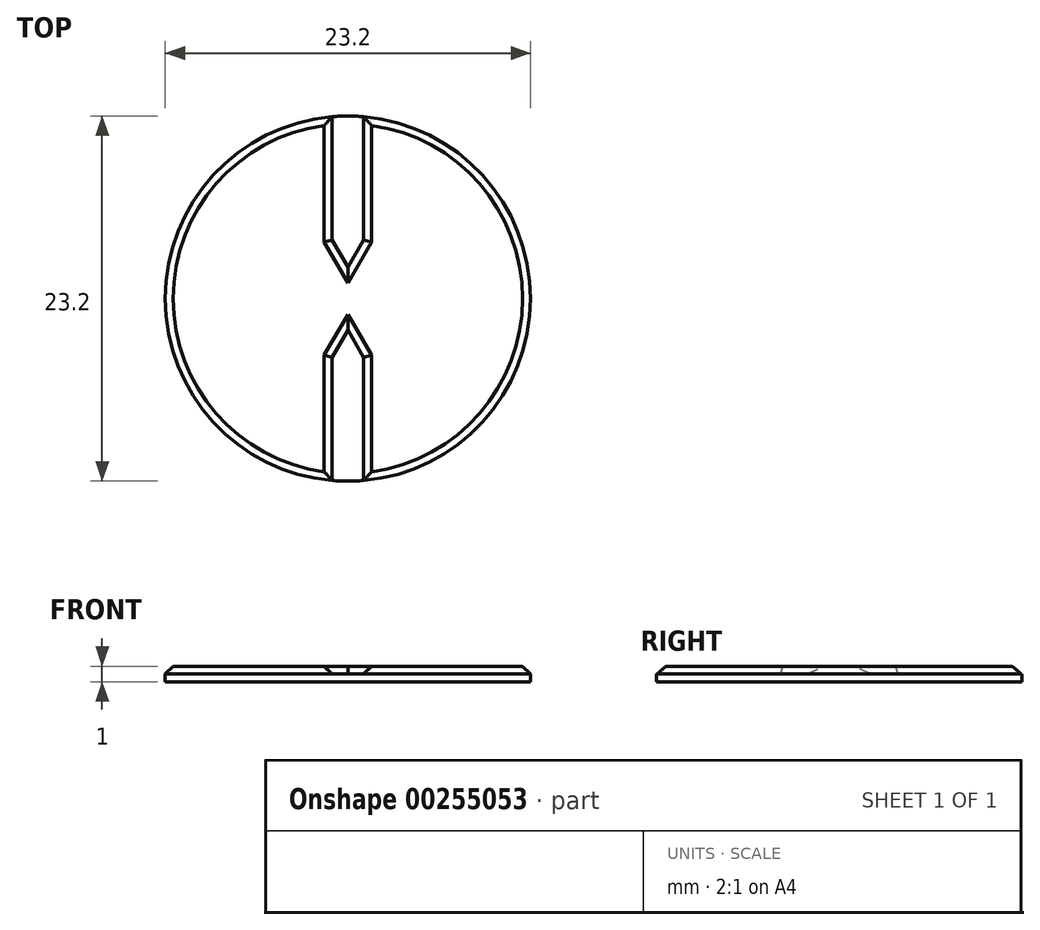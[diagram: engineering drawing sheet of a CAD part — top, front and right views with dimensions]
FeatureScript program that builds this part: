
annotation { "Feature Type Name" : "Feature", "Feature Type Description" : "" }
export const myFeature = defineFeature(function(context is Context, id is Id, definition is map)
    precondition{}
    {
        {
            var Q0;
            Q0=qCreatedBy(makeId("Top.planeOp"),FACE);
            var sketch = newSketch(context, id + "F0", { "sketchPlane" : qUnion([Q0])});
            skCircle(sketch, "E0", {"center": v(0, 0) * mm, "radius": 11.6 * mm});
            skSolve(sketch);
        }
        {
            var Q0;
            Q0 = qSketchRegion(id + "F0", true);
            extrude(context, id + "F1", {"entities" : qUnion([Q0]), "depth" : 1 * mm});
        }
        {
            var Q0;
            Q0=makeQuery(id+"F1.opExtrude","CAP_FACE",FACE,{"disambiguationData":[OSD([sQuery(id+"F0.wireOp",EDGE,"E0")])],"isStart":false});
            var sketch = newSketch(context, id + "F2", { "sketchPlane" : qUnion([Q0])});
            skLineSegment(sketch, "E1.bottom", {"start": v(1, -11.56) * mm, "end": v(-1, -11.56) * mm});
            skLineSegment(sketch, "E1.top", {"start": v(1, 11.56) * mm, "end": v(-1, 11.56) * mm});
            skLineSegment(sketch, "E1.left", {"start": v(1, -11.56) * mm, "end": v(1, 11.56) * mm});
            skLineSegment(sketch, "E1.right", {"start": v(-1, -11.56) * mm, "end": v(-1, 11.56) * mm});
            skPoint(sketch, "E1.middle", {"position": v(0, 0) * mm});
            skCircle(sketch, "E2.0.0", {"center": v(0, 0) * mm, "radius": 11.6 * mm});
            skLineSegment(sketch, "E3.1.0", {"start": v(4.91, -10.5) * mm, "end": v(-6.64, 9.5) * mm});
            skLineSegment(sketch, "E3.1.1", {"start": v(6.64, -9.5) * mm, "end": v(-4.91, 10.5) * mm});
            skLineSegment(sketch, "E3.2.0", {"start": v(9.5, -6.64) * mm, "end": v(-10.5, 4.91) * mm});
            skLineSegment(sketch, "E3.2.1", {"start": v(10.5, -4.91) * mm, "end": v(-9.5, 6.64) * mm});
            skLineSegment(sketch, "E3.3.0", {"start": v(11.56, -1) * mm, "end": v(-11.56, -1) * mm});
            skLineSegment(sketch, "E3.3.1", {"start": v(11.56, 1) * mm, "end": v(-11.56, 1) * mm});
            skLineSegment(sketch, "E3.4.0", {"start": v(10.5, 4.91) * mm, "end": v(-9.5, -6.64) * mm});
            skLineSegment(sketch, "E3.4.1", {"start": v(9.5, 6.64) * mm, "end": v(-10.5, -4.91) * mm});
            skLineSegment(sketch, "E3.5.0", {"start": v(6.64, 9.5) * mm, "end": v(-4.91, -10.5) * mm});
            skLineSegment(sketch, "E3.5.1", {"start": v(4.91, 10.5) * mm, "end": v(-6.64, -9.5) * mm});
            skLineSegment(sketch, "E3.6.0", {"start": v(1, 11.56) * mm, "end": v(1, -11.56) * mm});
            skLineSegment(sketch, "E3.6.1", {"start": v(-1, 11.56) * mm, "end": v(-1, -11.56) * mm});
            skLineSegment(sketch, "E3.7.0", {"start": v(-4.91, 10.5) * mm, "end": v(6.64, -9.5) * mm});
            skLineSegment(sketch, "E3.7.1", {"start": v(-6.64, 9.5) * mm, "end": v(4.91, -10.5) * mm});
            skLineSegment(sketch, "E3.8.0", {"start": v(-9.5, 6.64) * mm, "end": v(10.5, -4.91) * mm});
            skLineSegment(sketch, "E3.8.1", {"start": v(-10.5, 4.91) * mm, "end": v(9.5, -6.64) * mm});
            skLineSegment(sketch, "E3.9.0", {"start": v(-11.56, 1) * mm, "end": v(11.56, 1) * mm});
            skLineSegment(sketch, "E3.9.1", {"start": v(-11.56, -1) * mm, "end": v(11.56, -1) * mm});
            skLineSegment(sketch, "E3.10.0", {"start": v(-10.5, -4.91) * mm, "end": v(9.5, 6.64) * mm});
            skLineSegment(sketch, "E3.10.1", {"start": v(-9.5, -6.64) * mm, "end": v(10.5, 4.91) * mm});
            skLineSegment(sketch, "E3.11.0", {"start": v(-6.64, -9.5) * mm, "end": v(4.91, 10.5) * mm});
            skLineSegment(sketch, "E3.11.1", {"start": v(-4.91, -10.5) * mm, "end": v(6.64, 9.5) * mm});
            skSolve(sketch);
        }
        {
            var Q0;
            {var subQ1=sQuery(id+"F2.wireOp",EDGE,"E2.0.0");var subQ5=sQuery(id+"F2.wireOp",EDGE,"E3.7.0");var subQ9=makeQuery(id+"F2.imprint","INTERSECT",VERTEX,{"disambiguationData":[OD(0.0)],"derivedFrom":[subQ1,subQ5]});Q0=makeQuery(id+"F2.imprint","IMPRINT",FACE,{"disambiguationData":[TD([[makeQuery(id+"F2.imprint","IMPRINT",EDGE,{"disambiguationData":[TD([[subQ9,-1.0]])],"derivedFrom":subQ1}),1.0]])]});}
            var Q1;
            {var subQ1=sQuery(id+"F2.wireOp",EDGE,"E2.0.0");var subQ5=sQuery(id+"F2.wireOp",EDGE,"E3.8.0");var subQ6=makeQuery(id+"F2.imprint","INTERSECT",VERTEX,{"disambiguationData":[OD(0.0)],"derivedFrom":[subQ1,subQ5]});Q1=makeQuery(id+"F2.imprint","IMPRINT",FACE,{"disambiguationData":[TD([[makeQuery(id+"F2.imprint","IMPRINT",EDGE,{"disambiguationData":[TD([[subQ6,-1.0]])],"derivedFrom":subQ1}),1.0]])]});}
            var Q2;
            {var subQ1=sQuery(id+"F2.wireOp",EDGE,"E2.0.0");var subQ5=sQuery(id+"F2.wireOp",EDGE,"E3.9.0");var subQ6=makeQuery(id+"F2.imprint","INTERSECT",VERTEX,{"disambiguationData":[OD(0.0)],"derivedFrom":[subQ1,subQ5]});Q2=makeQuery(id+"F2.imprint","IMPRINT",FACE,{"disambiguationData":[TD([[makeQuery(id+"F2.imprint","IMPRINT",EDGE,{"disambiguationData":[TD([[subQ6,-1.0]])],"derivedFrom":subQ1}),1.0]])]});}
            var Q3;
            {var subQ1=sQuery(id+"F2.wireOp",EDGE,"E2.0.0");var subQ7=sQuery(id+"F2.wireOp",EDGE,"E3.10.0");var subQ8=makeQuery(id+"F2.imprint","INTERSECT",VERTEX,{"disambiguationData":[OD(0.0)],"derivedFrom":[subQ1,subQ7]});Q3=makeQuery(id+"F2.imprint","IMPRINT",FACE,{"disambiguationData":[TD([[makeQuery(id+"F2.imprint","IMPRINT",EDGE,{"disambiguationData":[TD([[subQ8,-1.0]])],"derivedFrom":subQ1}),1.0]])]});}
            var Q4;
            {var subQ0=sQuery(id+"F2.wireOp",EDGE,"E3.11.0");var subQ1=sQuery(id+"F2.wireOp",EDGE,"E2.0.0");var subQ2=makeQuery(id+"F2.imprint","INTERSECT",VERTEX,{"disambiguationData":[OD(0.0)],"derivedFrom":[subQ1,subQ0]});Q4=makeQuery(id+"F2.imprint","IMPRINT",FACE,{"disambiguationData":[TD([[makeQuery(id+"F2.imprint","IMPRINT",EDGE,{"disambiguationData":[TD([[subQ2,-1.0]])],"derivedFrom":subQ1}),1.0]])]});}
            var Q5;
            {var subQ7=sQuery(id+"F2.wireOp",EDGE,"E1.bottom");Q5=makeQuery(id+"F2.imprint","IMPRINT",FACE,{"disambiguationData":[TD([[makeQuery(id+"F2.imprint","IMPRINT",EDGE,{"derivedFrom":subQ7}),-1.0]])]});}
            var Q6;
            {var subQ1=sQuery(id+"F2.wireOp",EDGE,"E2.0.0");var subQ5=sQuery(id+"F2.wireOp",EDGE,"E3.7.0");var subQ6=makeQuery(id+"F2.imprint","INTERSECT",VERTEX,{"disambiguationData":[OD(1.0)],"derivedFrom":[subQ1,subQ5]});Q6=makeQuery(id+"F2.imprint","IMPRINT",FACE,{"disambiguationData":[TD([[makeQuery(id+"F2.imprint","IMPRINT",EDGE,{"disambiguationData":[TD([[subQ6,1.0]])],"derivedFrom":subQ1}),1.0]])]});}
            var Q7;
            {var subQ0=sQuery(id+"F2.wireOp",EDGE,"E3.8.0");var subQ1=sQuery(id+"F2.wireOp",EDGE,"E2.0.0");var subQ2=makeQuery(id+"F2.imprint","INTERSECT",VERTEX,{"disambiguationData":[OD(1.0)],"derivedFrom":[subQ1,subQ0]});Q7=makeQuery(id+"F2.imprint","IMPRINT",FACE,{"disambiguationData":[TD([[makeQuery(id+"F2.imprint","IMPRINT",EDGE,{"disambiguationData":[TD([[subQ2,1.0]])],"derivedFrom":subQ1}),1.0]])]});}
            var Q8;
            {var subQ1=sQuery(id+"F2.wireOp",EDGE,"E2.0.0");var subQ5=sQuery(id+"F2.wireOp",EDGE,"E3.9.0");var subQ6=makeQuery(id+"F2.imprint","INTERSECT",VERTEX,{"disambiguationData":[OD(1.0)],"derivedFrom":[subQ1,subQ5]});Q8=makeQuery(id+"F2.imprint","IMPRINT",FACE,{"disambiguationData":[TD([[makeQuery(id+"F2.imprint","IMPRINT",EDGE,{"disambiguationData":[TD([[subQ6,1.0]])],"derivedFrom":subQ1}),1.0]])]});}
            var Q9;
            {var subQ1=sQuery(id+"F2.wireOp",EDGE,"E2.0.0");var subQ5=sQuery(id+"F2.wireOp",EDGE,"E3.10.0");var subQ6=makeQuery(id+"F2.imprint","INTERSECT",VERTEX,{"disambiguationData":[OD(1.0)],"derivedFrom":[subQ1,subQ5]});Q9=makeQuery(id+"F2.imprint","IMPRINT",FACE,{"disambiguationData":[TD([[makeQuery(id+"F2.imprint","IMPRINT",EDGE,{"disambiguationData":[TD([[subQ6,1.0]])],"derivedFrom":subQ1}),1.0]])]});}
            var Q10;
            {var subQ0=sQuery(id+"F2.wireOp",EDGE,"E3.11.0");var subQ1=sQuery(id+"F2.wireOp",EDGE,"E2.0.0");var subQ2=makeQuery(id+"F2.imprint","INTERSECT",VERTEX,{"disambiguationData":[OD(1.0)],"derivedFrom":[subQ1,subQ0]});Q10=makeQuery(id+"F2.imprint","IMPRINT",FACE,{"disambiguationData":[TD([[makeQuery(id+"F2.imprint","IMPRINT",EDGE,{"disambiguationData":[TD([[subQ2,1.0]])],"derivedFrom":subQ1}),1.0]])]});}
            var Q11;
            {var subQ6=sQuery(id+"F2.wireOp",EDGE,"E1.top");Q11=makeQuery(id+"F2.imprint","IMPRINT",FACE,{"disambiguationData":[TD([[makeQuery(id+"F2.imprint","IMPRINT",EDGE,{"derivedFrom":subQ6}),1.0]])]});}
            var Q12;
            {var subQ0=sQuery(id+"F2.wireOp",EDGE,"E3.7.0");var subQ1=sQuery(id+"F2.wireOp",EDGE,"E3.6.1");var subQ2=makeQuery(id+"F2.imprint","INTERSECT",VERTEX,{"derivedFrom":[subQ1,subQ0]});Q12=makeQuery(id+"F2.imprint","IMPRINT",FACE,{"disambiguationData":[TD([[makeQuery(id+"F2.imprint","IMPRINT",EDGE,{"disambiguationData":[TD([[subQ2,-1.0]])],"derivedFrom":subQ1}),1.0]])]});}
            var Q13;
            {var subQ0=sQuery(id+"F2.wireOp",EDGE,"E3.9.0");var subQ1=sQuery(id+"F2.wireOp",EDGE,"E3.7.1");var subQ2=makeQuery(id+"F2.imprint","INTERSECT",VERTEX,{"derivedFrom":[subQ1,subQ0]});Q13=makeQuery(id+"F2.imprint","IMPRINT",FACE,{"disambiguationData":[TD([[makeQuery(id+"F2.imprint","IMPRINT",EDGE,{"disambiguationData":[TD([[subQ2,-1.0]])],"derivedFrom":subQ1}),-1.0]])]});}
            var Q14;
            {var subQ0=sQuery(id+"F2.wireOp",EDGE,"E3.10.0");var subQ1=sQuery(id+"F2.wireOp",EDGE,"E3.8.1");var subQ2=makeQuery(id+"F2.imprint","INTERSECT",VERTEX,{"derivedFrom":[subQ1,subQ0]});Q14=makeQuery(id+"F2.imprint","IMPRINT",FACE,{"disambiguationData":[TD([[makeQuery(id+"F2.imprint","IMPRINT",EDGE,{"disambiguationData":[TD([[subQ2,-1.0]])],"derivedFrom":subQ1}),-1.0]])]});}
            var Q15;
            {var subQ0=sQuery(id+"F2.wireOp",EDGE,"E3.8.1");var subQ1=sQuery(id+"F2.wireOp",EDGE,"E3.6.1");var subQ2=makeQuery(id+"F2.imprint","INTERSECT",VERTEX,{"derivedFrom":[subQ1,subQ0]});Q15=makeQuery(id+"F2.imprint","IMPRINT",FACE,{"disambiguationData":[TD([[makeQuery(id+"F2.imprint","IMPRINT",EDGE,{"disambiguationData":[TD([[subQ2,-1.0]])],"derivedFrom":subQ1}),-1.0]])]});}
            var Q16;
            {var subQ0=sQuery(id+"F2.wireOp",EDGE,"E3.9.1");var subQ1=sQuery(id+"F2.wireOp",EDGE,"E3.6.1");var subQ2=makeQuery(id+"F2.imprint","INTERSECT",VERTEX,{"derivedFrom":[subQ1,subQ0]});Q16=makeQuery(id+"F2.imprint","IMPRINT",FACE,{"disambiguationData":[TD([[makeQuery(id+"F2.imprint","IMPRINT",EDGE,{"disambiguationData":[TD([[subQ2,-1.0]])],"derivedFrom":subQ1}),1.0]])]});}
            var Q17;
            {var subQ0=sQuery(id+"F2.wireOp",EDGE,"E3.10.1");var subQ1=sQuery(id+"F2.wireOp",EDGE,"E3.6.1");var subQ2=makeQuery(id+"F2.imprint","INTERSECT",VERTEX,{"derivedFrom":[subQ1,subQ0]});Q17=makeQuery(id+"F2.imprint","IMPRINT",FACE,{"disambiguationData":[TD([[makeQuery(id+"F2.imprint","IMPRINT",EDGE,{"disambiguationData":[TD([[subQ2,-1.0]])],"derivedFrom":subQ1}),1.0]])]});}
            var Q18;
            {var subQ0=sQuery(id+"F2.wireOp",EDGE,"E3.10.1");var subQ1=sQuery(id+"F2.wireOp",EDGE,"E3.7.1");var subQ2=makeQuery(id+"F2.imprint","INTERSECT",VERTEX,{"derivedFrom":[subQ1,subQ0]});Q18=makeQuery(id+"F2.imprint","IMPRINT",FACE,{"disambiguationData":[TD([[makeQuery(id+"F2.imprint","IMPRINT",EDGE,{"disambiguationData":[TD([[subQ2,-1.0]])],"derivedFrom":subQ1}),1.0]])]});}
            var Q19;
            {var subQ0=sQuery(id+"F2.wireOp",EDGE,"E3.8.1");var subQ1=sQuery(id+"F2.wireOp",EDGE,"E3.6.0");var subQ2=makeQuery(id+"F2.imprint","INTERSECT",VERTEX,{"derivedFrom":[subQ1,subQ0]});Q19=makeQuery(id+"F2.imprint","IMPRINT",FACE,{"disambiguationData":[TD([[makeQuery(id+"F2.imprint","IMPRINT",EDGE,{"disambiguationData":[TD([[subQ2,-1.0]])],"derivedFrom":subQ1}),-1.0]])]});}
            var Q20;
            {var subQ0=sQuery(id+"F2.wireOp",EDGE,"E3.9.1");var subQ1=sQuery(id+"F2.wireOp",EDGE,"E3.6.0");var subQ2=makeQuery(id+"F2.imprint","INTERSECT",VERTEX,{"derivedFrom":[subQ1,subQ0]});Q20=makeQuery(id+"F2.imprint","IMPRINT",FACE,{"disambiguationData":[TD([[makeQuery(id+"F2.imprint","IMPRINT",EDGE,{"disambiguationData":[TD([[subQ2,-1.0]])],"derivedFrom":subQ1}),-1.0]])]});}
            var Q21;
            {var subQ0=sQuery(id+"F2.wireOp",EDGE,"E3.10.1");var subQ1=sQuery(id+"F2.wireOp",EDGE,"E3.6.0");var subQ2=makeQuery(id+"F2.imprint","INTERSECT",VERTEX,{"derivedFrom":[subQ1,subQ0]});Q21=makeQuery(id+"F2.imprint","IMPRINT",FACE,{"disambiguationData":[TD([[makeQuery(id+"F2.imprint","IMPRINT",EDGE,{"disambiguationData":[TD([[subQ2,-1.0]])],"derivedFrom":subQ1}),1.0]])]});}
            var Q22;
            {var subQ0=sQuery(id+"F2.wireOp",EDGE,"E3.10.1");var subQ1=sQuery(id+"F2.wireOp",EDGE,"E3.7.0");var subQ2=makeQuery(id+"F2.imprint","INTERSECT",VERTEX,{"derivedFrom":[subQ1,subQ0]});Q22=makeQuery(id+"F2.imprint","IMPRINT",FACE,{"disambiguationData":[TD([[makeQuery(id+"F2.imprint","IMPRINT",EDGE,{"disambiguationData":[TD([[subQ2,-1.0]])],"derivedFrom":subQ1}),1.0]])]});}
            var Q23;
            {var subQ0=sQuery(id+"F2.wireOp",EDGE,"E3.11.1");var subQ1=sQuery(id+"F2.wireOp",EDGE,"E3.7.0");var subQ2=makeQuery(id+"F2.imprint","INTERSECT",VERTEX,{"derivedFrom":[subQ1,subQ0]});Q23=makeQuery(id+"F2.imprint","IMPRINT",FACE,{"disambiguationData":[TD([[makeQuery(id+"F2.imprint","IMPRINT",EDGE,{"disambiguationData":[TD([[subQ2,-1.0]])],"derivedFrom":subQ1}),1.0]])]});}
            var Q24;
            {var subQ0=sQuery(id+"F2.wireOp",EDGE,"E3.9.0");var subQ1=sQuery(id+"F2.wireOp",EDGE,"E3.6.0");var subQ2=makeQuery(id+"F2.imprint","INTERSECT",VERTEX,{"derivedFrom":[subQ1,subQ0]});Q24=makeQuery(id+"F2.imprint","IMPRINT",FACE,{"disambiguationData":[TD([[makeQuery(id+"F2.imprint","IMPRINT",EDGE,{"disambiguationData":[TD([[subQ2,-1.0]])],"derivedFrom":subQ1}),1.0]])]});}
            var Q25;
            {var subQ0=sQuery(id+"F2.wireOp",EDGE,"E3.9.0");var subQ1=sQuery(id+"F2.wireOp",EDGE,"E3.6.0");var subQ2=makeQuery(id+"F2.imprint","INTERSECT",VERTEX,{"derivedFrom":[subQ1,subQ0]});Q25=makeQuery(id+"F2.imprint","IMPRINT",FACE,{"disambiguationData":[TD([[makeQuery(id+"F2.imprint","IMPRINT",EDGE,{"disambiguationData":[TD([[subQ2,-1.0]])],"derivedFrom":subQ1}),-1.0]])]});}
            var Q26;
            {var subQ0=sQuery(id+"F2.wireOp",EDGE,"E3.10.0");var subQ1=sQuery(id+"F2.wireOp",EDGE,"E3.6.0");var subQ2=makeQuery(id+"F2.imprint","INTERSECT",VERTEX,{"derivedFrom":[subQ1,subQ0]});Q26=makeQuery(id+"F2.imprint","IMPRINT",FACE,{"disambiguationData":[TD([[makeQuery(id+"F2.imprint","IMPRINT",EDGE,{"disambiguationData":[TD([[subQ2,-1.0]])],"derivedFrom":subQ1}),-1.0]])]});}
            var Q27;
            {var subQ0=sQuery(id+"F2.wireOp",EDGE,"E3.10.0");var subQ1=sQuery(id+"F2.wireOp",EDGE,"E3.7.0");var subQ2=makeQuery(id+"F2.imprint","INTERSECT",VERTEX,{"derivedFrom":[subQ1,subQ0]});Q27=makeQuery(id+"F2.imprint","IMPRINT",FACE,{"disambiguationData":[TD([[makeQuery(id+"F2.imprint","IMPRINT",EDGE,{"disambiguationData":[TD([[subQ2,-1.0]])],"derivedFrom":subQ1}),-1.0]])]});}
            var Q28;
            {var subQ0=sQuery(id+"F2.wireOp",EDGE,"E3.11.0");var subQ1=sQuery(id+"F2.wireOp",EDGE,"E3.7.0");var subQ2=makeQuery(id+"F2.imprint","INTERSECT",VERTEX,{"derivedFrom":[subQ1,subQ0]});Q28=makeQuery(id+"F2.imprint","IMPRINT",FACE,{"disambiguationData":[TD([[makeQuery(id+"F2.imprint","IMPRINT",EDGE,{"disambiguationData":[TD([[subQ2,-1.0]])],"derivedFrom":subQ1}),-1.0]])]});}
            var Q29;
            {var subQ0=sQuery(id+"F2.wireOp",EDGE,"E3.8.0");var subQ1=sQuery(id+"F2.wireOp",EDGE,"E3.6.1");var subQ2=makeQuery(id+"F2.imprint","INTERSECT",VERTEX,{"derivedFrom":[subQ1,subQ0]});Q29=makeQuery(id+"F2.imprint","IMPRINT",FACE,{"disambiguationData":[TD([[makeQuery(id+"F2.imprint","IMPRINT",EDGE,{"disambiguationData":[TD([[subQ2,-1.0]])],"derivedFrom":subQ1}),1.0]])]});}
            var Q30;
            {var subQ0=sQuery(id+"F2.wireOp",EDGE,"E3.9.0");var subQ1=sQuery(id+"F2.wireOp",EDGE,"E3.6.1");var subQ2=makeQuery(id+"F2.imprint","INTERSECT",VERTEX,{"derivedFrom":[subQ1,subQ0]});Q30=makeQuery(id+"F2.imprint","IMPRINT",FACE,{"disambiguationData":[TD([[makeQuery(id+"F2.imprint","IMPRINT",EDGE,{"disambiguationData":[TD([[subQ2,-1.0]])],"derivedFrom":subQ1}),-1.0]])]});}
            var Q31;
            {var subQ0=sQuery(id+"F2.wireOp",EDGE,"E3.9.0");var subQ1=sQuery(id+"F2.wireOp",EDGE,"E3.6.1");var subQ2=makeQuery(id+"F2.imprint","INTERSECT",VERTEX,{"derivedFrom":[subQ1,subQ0]});Q31=makeQuery(id+"F2.imprint","IMPRINT",FACE,{"disambiguationData":[TD([[makeQuery(id+"F2.imprint","IMPRINT",EDGE,{"disambiguationData":[TD([[subQ2,-1.0]])],"derivedFrom":subQ1}),1.0]])]});}
            var Q32;
            {var subQ0=sQuery(id+"F2.wireOp",EDGE,"E3.11.0");var subQ1=sQuery(id+"F2.wireOp",EDGE,"E3.8.0");var subQ2=makeQuery(id+"F2.imprint","INTERSECT",VERTEX,{"derivedFrom":[subQ1,subQ0]});Q32=makeQuery(id+"F2.imprint","IMPRINT",FACE,{"disambiguationData":[TD([[makeQuery(id+"F2.imprint","IMPRINT",EDGE,{"disambiguationData":[TD([[subQ2,-1.0]])],"derivedFrom":subQ1}),-1.0]])]});}
            var Q33;
            {var subQ0=sQuery(id+"F2.wireOp",EDGE,"E3.10.0");var subQ1=sQuery(id+"F2.wireOp",EDGE,"E3.6.1");var subQ2=makeQuery(id+"F2.imprint","INTERSECT",VERTEX,{"derivedFrom":[subQ1,subQ0]});Q33=makeQuery(id+"F2.imprint","IMPRINT",FACE,{"disambiguationData":[TD([[makeQuery(id+"F2.imprint","IMPRINT",EDGE,{"disambiguationData":[TD([[subQ2,-1.0]])],"derivedFrom":subQ1}),-1.0]])]});}
            var Q34;
            {var subQ0=sQuery(id+"F2.wireOp",EDGE,"E3.7.1");var subQ1=sQuery(id+"F2.wireOp",EDGE,"E3.6.1");var subQ2=makeQuery(id+"F2.imprint","INTERSECT",VERTEX,{"derivedFrom":[subQ1,subQ0]});Q34=makeQuery(id+"F2.imprint","IMPRINT",FACE,{"disambiguationData":[TD([[makeQuery(id+"F2.imprint","IMPRINT",EDGE,{"disambiguationData":[TD([[subQ2,-1.0]])],"derivedFrom":subQ1}),-1.0]])]});}
            var Q35;
            {var subQ0=sQuery(id+"F2.wireOp",EDGE,"E3.11.0");var subQ1=sQuery(id+"F2.wireOp",EDGE,"E3.6.1");var subQ2=makeQuery(id+"F2.imprint","INTERSECT",VERTEX,{"derivedFrom":[subQ1,subQ0]});Q35=makeQuery(id+"F2.imprint","IMPRINT",FACE,{"disambiguationData":[TD([[makeQuery(id+"F2.imprint","IMPRINT",EDGE,{"disambiguationData":[TD([[subQ2,-1.0]])],"derivedFrom":subQ1}),-1.0]])]});}
            var Q36;
            {var subQ7=sQuery(id+"F2.wireOp",EDGE,"E3.7.0");var subQ8=sQuery(id+"F2.wireOp",EDGE,"E3.6.0");var subQ9=makeQuery(id+"F2.imprint","INTERSECT",VERTEX,{"derivedFrom":[subQ8,subQ7]});Q36=makeQuery(id+"F2.imprint","IMPRINT",FACE,{"disambiguationData":[TD([[makeQuery(id+"F2.imprint","IMPRINT",EDGE,{"disambiguationData":[TD([[subQ9,-1.0]])],"derivedFrom":subQ8}),-1.0]])]});}
            var Q37;
            {var subQ0=sQuery(id+"F2.wireOp",EDGE,"E3.7.1");var subQ1=sQuery(id+"F2.wireOp",EDGE,"E3.6.1");var subQ2=makeQuery(id+"F2.imprint","INTERSECT",VERTEX,{"derivedFrom":[subQ1,subQ0]});Q37=makeQuery(id+"F2.imprint","IMPRINT",FACE,{"disambiguationData":[TD([[makeQuery(id+"F2.imprint","IMPRINT",EDGE,{"disambiguationData":[TD([[subQ2,-1.0]])],"derivedFrom":subQ1}),1.0]])]});}
            var Q38;
            {var subQ0=sQuery(id+"F2.wireOp",EDGE,"E3.8.1");var subQ1=sQuery(id+"F2.wireOp",EDGE,"E3.7.1");var subQ2=makeQuery(id+"F2.imprint","INTERSECT",VERTEX,{"derivedFrom":[subQ1,subQ0]});Q38=makeQuery(id+"F2.imprint","IMPRINT",FACE,{"disambiguationData":[TD([[makeQuery(id+"F2.imprint","IMPRINT",EDGE,{"disambiguationData":[TD([[subQ2,-1.0]])],"derivedFrom":subQ1}),1.0]])]});}
            var Q39;
            {var subQ0=sQuery(id+"F2.wireOp",EDGE,"E3.9.1");var subQ1=sQuery(id+"F2.wireOp",EDGE,"E3.8.1");var subQ2=makeQuery(id+"F2.imprint","INTERSECT",VERTEX,{"derivedFrom":[subQ1,subQ0]});Q39=makeQuery(id+"F2.imprint","IMPRINT",FACE,{"disambiguationData":[TD([[makeQuery(id+"F2.imprint","IMPRINT",EDGE,{"disambiguationData":[TD([[subQ2,-1.0]])],"derivedFrom":subQ1}),1.0]])]});}
            var Q40;
            {var subQ0=sQuery(id+"F2.wireOp",EDGE,"E3.10.1");var subQ1=sQuery(id+"F2.wireOp",EDGE,"E3.9.1");var subQ2=makeQuery(id+"F2.imprint","INTERSECT",VERTEX,{"derivedFrom":[subQ1,subQ0]});Q40=makeQuery(id+"F2.imprint","IMPRINT",FACE,{"disambiguationData":[TD([[makeQuery(id+"F2.imprint","IMPRINT",EDGE,{"disambiguationData":[TD([[subQ2,-1.0]])],"derivedFrom":subQ1}),1.0]])]});}
            var Q41;
            {var subQ0=sQuery(id+"F2.wireOp",EDGE,"E3.11.1");var subQ1=sQuery(id+"F2.wireOp",EDGE,"E3.6.0");var subQ2=makeQuery(id+"F2.imprint","INTERSECT",VERTEX,{"derivedFrom":[subQ1,subQ0]});Q41=makeQuery(id+"F2.imprint","IMPRINT",FACE,{"disambiguationData":[TD([[makeQuery(id+"F2.imprint","IMPRINT",EDGE,{"disambiguationData":[TD([[subQ2,-1.0]])],"derivedFrom":subQ1}),-1.0]])]});}
            var Q42;
            {var subQ0=sQuery(id+"F2.wireOp",EDGE,"E3.7.0");var subQ1=sQuery(id+"F2.wireOp",EDGE,"E3.6.0");var subQ2=makeQuery(id+"F2.imprint","INTERSECT",VERTEX,{"derivedFrom":[subQ1,subQ0]});Q42=makeQuery(id+"F2.imprint","IMPRINT",FACE,{"disambiguationData":[TD([[makeQuery(id+"F2.imprint","IMPRINT",EDGE,{"disambiguationData":[TD([[subQ2,-1.0]])],"derivedFrom":subQ1}),1.0]])]});}
            var Q43;
            {var subQ0=sQuery(id+"F2.wireOp",EDGE,"E3.8.0");var subQ1=sQuery(id+"F2.wireOp",EDGE,"E3.6.0");var subQ2=makeQuery(id+"F2.imprint","INTERSECT",VERTEX,{"derivedFrom":[subQ1,subQ0]});Q43=makeQuery(id+"F2.imprint","IMPRINT",FACE,{"disambiguationData":[TD([[makeQuery(id+"F2.imprint","IMPRINT",EDGE,{"disambiguationData":[TD([[subQ2,-1.0]])],"derivedFrom":subQ1}),-1.0]])]});}
            var Q44;
            {var subQ0=sQuery(id+"F2.wireOp",EDGE,"E3.8.0");var subQ1=sQuery(id+"F2.wireOp",EDGE,"E3.6.0");var subQ2=makeQuery(id+"F2.imprint","INTERSECT",VERTEX,{"derivedFrom":[subQ1,subQ0]});Q44=makeQuery(id+"F2.imprint","IMPRINT",FACE,{"disambiguationData":[TD([[makeQuery(id+"F2.imprint","IMPRINT",EDGE,{"disambiguationData":[TD([[subQ2,-1.0]])],"derivedFrom":subQ1}),1.0]])]});}
            var Q45;
            {var subQ0=sQuery(id+"F2.wireOp",EDGE,"E3.11.0");var subQ1=sQuery(id+"F2.wireOp",EDGE,"E3.6.0");var subQ2=makeQuery(id+"F2.imprint","INTERSECT",VERTEX,{"derivedFrom":[subQ1,subQ0]});Q45=makeQuery(id+"F2.imprint","IMPRINT",FACE,{"disambiguationData":[TD([[makeQuery(id+"F2.imprint","IMPRINT",EDGE,{"disambiguationData":[TD([[subQ2,-1.0]])],"derivedFrom":subQ1}),-1.0]])]});}
            var Q46;
            {var subQ0=sQuery(id+"F2.wireOp",EDGE,"E3.10.0");var subQ1=sQuery(id+"F2.wireOp",EDGE,"E3.6.0");var subQ2=makeQuery(id+"F2.imprint","INTERSECT",VERTEX,{"derivedFrom":[subQ1,subQ0]});Q46=makeQuery(id+"F2.imprint","IMPRINT",FACE,{"disambiguationData":[TD([[makeQuery(id+"F2.imprint","IMPRINT",EDGE,{"disambiguationData":[TD([[subQ2,-1.0]])],"derivedFrom":subQ1}),1.0]])]});}
            var Q47;
            {var subQ0=sQuery(id+"F2.wireOp",EDGE,"E3.11.1");var subQ1=sQuery(id+"F2.wireOp",EDGE,"E3.8.0");var subQ2=makeQuery(id+"F2.imprint","INTERSECT",VERTEX,{"derivedFrom":[subQ1,subQ0]});Q47=makeQuery(id+"F2.imprint","IMPRINT",FACE,{"disambiguationData":[TD([[makeQuery(id+"F2.imprint","IMPRINT",EDGE,{"disambiguationData":[TD([[subQ2,-1.0]])],"derivedFrom":subQ1}),1.0]])]});}
            var Q48;
            {var subQ0=sQuery(id+"F2.wireOp",EDGE,"E3.9.1");var subQ1=sQuery(id+"F2.wireOp",EDGE,"E3.6.0");var subQ2=makeQuery(id+"F2.imprint","INTERSECT",VERTEX,{"derivedFrom":[subQ1,subQ0]});Q48=makeQuery(id+"F2.imprint","IMPRINT",FACE,{"disambiguationData":[TD([[makeQuery(id+"F2.imprint","IMPRINT",EDGE,{"disambiguationData":[TD([[subQ2,-1.0]])],"derivedFrom":subQ1}),1.0]])]});}
            var Q49;
            {var subQ0=sQuery(id+"F2.wireOp",EDGE,"E3.9.1");var subQ1=sQuery(id+"F2.wireOp",EDGE,"E3.6.1");var subQ2=makeQuery(id+"F2.imprint","INTERSECT",VERTEX,{"derivedFrom":[subQ1,subQ0]});Q49=makeQuery(id+"F2.imprint","IMPRINT",FACE,{"disambiguationData":[TD([[makeQuery(id+"F2.imprint","IMPRINT",EDGE,{"disambiguationData":[TD([[subQ2,-1.0]])],"derivedFrom":subQ1}),-1.0]])]});}
            var Q50;
            {var subQ0=sQuery(id+"F2.wireOp",EDGE,"E3.10.0");var subQ1=sQuery(id+"F2.wireOp",EDGE,"E3.7.1");var subQ2=makeQuery(id+"F2.imprint","INTERSECT",VERTEX,{"derivedFrom":[subQ1,subQ0]});Q50=makeQuery(id+"F2.imprint","IMPRINT",FACE,{"disambiguationData":[TD([[makeQuery(id+"F2.imprint","IMPRINT",EDGE,{"disambiguationData":[TD([[subQ2,-1.0]])],"derivedFrom":subQ1}),-1.0]])]});}
            var Q51;
            {var subQ0=sQuery(id+"F2.wireOp",EDGE,"E3.8.0");var subQ1=sQuery(id+"F2.wireOp",EDGE,"E3.6.1");var subQ2=makeQuery(id+"F2.imprint","INTERSECT",VERTEX,{"derivedFrom":[subQ1,subQ0]});Q51=makeQuery(id+"F2.imprint","IMPRINT",FACE,{"disambiguationData":[TD([[makeQuery(id+"F2.imprint","IMPRINT",EDGE,{"disambiguationData":[TD([[subQ2,-1.0]])],"derivedFrom":subQ1}),-1.0]])]});}
            var Q52;
            {var subQ0=sQuery(id+"F2.wireOp",EDGE,"E3.10.0");var subQ1=sQuery(id+"F2.wireOp",EDGE,"E3.6.1");var subQ2=makeQuery(id+"F2.imprint","INTERSECT",VERTEX,{"derivedFrom":[subQ1,subQ0]});Q52=makeQuery(id+"F2.imprint","IMPRINT",FACE,{"disambiguationData":[TD([[makeQuery(id+"F2.imprint","IMPRINT",EDGE,{"disambiguationData":[TD([[subQ2,-1.0]])],"derivedFrom":subQ1}),1.0]])]});}
            var Q53;
            {var subQ0=sQuery(id+"F2.wireOp",EDGE,"E3.11.0");var subQ1=sQuery(id+"F2.wireOp",EDGE,"E3.9.0");var subQ2=makeQuery(id+"F2.imprint","INTERSECT",VERTEX,{"derivedFrom":[subQ1,subQ0]});Q53=makeQuery(id+"F2.imprint","IMPRINT",FACE,{"disambiguationData":[TD([[makeQuery(id+"F2.imprint","IMPRINT",EDGE,{"disambiguationData":[TD([[subQ2,-1.0]])],"derivedFrom":subQ1}),-1.0]])]});}
            var Q54;
            {var subQ0=sQuery(id+"F2.wireOp",EDGE,"E3.10.0");var subQ1=sQuery(id+"F2.wireOp",EDGE,"E3.8.0");var subQ2=makeQuery(id+"F2.imprint","INTERSECT",VERTEX,{"derivedFrom":[subQ1,subQ0]});Q54=makeQuery(id+"F2.imprint","IMPRINT",FACE,{"disambiguationData":[TD([[makeQuery(id+"F2.imprint","IMPRINT",EDGE,{"disambiguationData":[TD([[subQ2,-1.0]])],"derivedFrom":subQ1}),-1.0]])]});}
            var Q55;
            {var subQ0=sQuery(id+"F2.wireOp",EDGE,"E3.9.0");var subQ1=sQuery(id+"F2.wireOp",EDGE,"E3.7.0");var subQ2=makeQuery(id+"F2.imprint","INTERSECT",VERTEX,{"derivedFrom":[subQ1,subQ0]});Q55=makeQuery(id+"F2.imprint","IMPRINT",FACE,{"disambiguationData":[TD([[makeQuery(id+"F2.imprint","IMPRINT",EDGE,{"disambiguationData":[TD([[subQ2,-1.0]])],"derivedFrom":subQ1}),-1.0]])]});}
            var Q56;
            {var subQ0=sQuery(id+"F2.wireOp",EDGE,"E3.11.1");var subQ1=sQuery(id+"F2.wireOp",EDGE,"E3.6.0");var subQ2=makeQuery(id+"F2.imprint","INTERSECT",VERTEX,{"derivedFrom":[subQ1,subQ0]});Q56=makeQuery(id+"F2.imprint","IMPRINT",FACE,{"disambiguationData":[TD([[makeQuery(id+"F2.imprint","IMPRINT",EDGE,{"disambiguationData":[TD([[subQ2,-1.0]])],"derivedFrom":subQ1}),1.0]])]});}
            var Q57;
            {var subQ0=sQuery(id+"F2.wireOp",EDGE,"E3.10.1");var subQ1=sQuery(id+"F2.wireOp",EDGE,"E3.6.0");var subQ2=makeQuery(id+"F2.imprint","INTERSECT",VERTEX,{"derivedFrom":[subQ1,subQ0]});Q57=makeQuery(id+"F2.imprint","IMPRINT",FACE,{"disambiguationData":[TD([[makeQuery(id+"F2.imprint","IMPRINT",EDGE,{"disambiguationData":[TD([[subQ2,-1.0]])],"derivedFrom":subQ1}),-1.0]])]});}
            var Q58;
            {var subQ0=sQuery(id+"F2.wireOp",EDGE,"E3.10.1");var subQ1=sQuery(id+"F2.wireOp",EDGE,"E3.8.1");var subQ2=makeQuery(id+"F2.imprint","INTERSECT",VERTEX,{"derivedFrom":[subQ1,subQ0]});Q58=makeQuery(id+"F2.imprint","IMPRINT",FACE,{"disambiguationData":[TD([[makeQuery(id+"F2.imprint","IMPRINT",EDGE,{"disambiguationData":[TD([[subQ2,-1.0]])],"derivedFrom":subQ1}),1.0]])]});}
            var Q59;
            {var subQ0=sQuery(id+"F2.wireOp",EDGE,"E3.9.1");var subQ1=sQuery(id+"F2.wireOp",EDGE,"E3.7.1");var subQ2=makeQuery(id+"F2.imprint","INTERSECT",VERTEX,{"derivedFrom":[subQ1,subQ0]});Q59=makeQuery(id+"F2.imprint","IMPRINT",FACE,{"disambiguationData":[TD([[makeQuery(id+"F2.imprint","IMPRINT",EDGE,{"disambiguationData":[TD([[subQ2,-1.0]])],"derivedFrom":subQ1}),1.0]])]});}
            var Q60;
            {var subQ0=sQuery(id+"F2.wireOp",EDGE,"E3.8.1");var subQ1=sQuery(id+"F2.wireOp",EDGE,"E3.6.1");var subQ2=makeQuery(id+"F2.imprint","INTERSECT",VERTEX,{"derivedFrom":[subQ1,subQ0]});Q60=makeQuery(id+"F2.imprint","IMPRINT",FACE,{"disambiguationData":[TD([[makeQuery(id+"F2.imprint","IMPRINT",EDGE,{"disambiguationData":[TD([[subQ2,-1.0]])],"derivedFrom":subQ1}),1.0]])]});}
            var Q61;
            {var subQ0=sQuery(id+"F2.wireOp",EDGE,"E1.top");Q61=makeQuery(id+"F2.imprint","IMPRINT",FACE,{"disambiguationData":[TD([[makeQuery(id+"F2.imprint","IMPRINT",EDGE,{"derivedFrom":subQ0}),-1.0]])]});}
            var Q62;
            {var subQ0=sQuery(id+"F2.wireOp",EDGE,"E1.bottom");Q62=makeQuery(id+"F2.imprint","IMPRINT",FACE,{"disambiguationData":[TD([[makeQuery(id+"F2.imprint","IMPRINT",EDGE,{"derivedFrom":subQ0}),1.0]])]});}
            extrude(context, id + "F3", {"entities" : qUnion([Q0, Q1, Q2, Q3, Q4, Q5, Q6, Q7, Q8, Q9, Q10, Q11, Q12, Q13, Q14, Q15, Q16, Q17, Q18, Q19, Q20, Q21, Q22, Q23, Q24, Q25, Q26, Q27, Q28, Q29, Q30, Q31, Q32, Q33, Q34, Q35, Q36, Q37, Q38, Q39, Q40, Q41, Q42, Q43, Q44, Q45, Q46, Q47, Q48, Q49, Q50, Q51, Q52, Q53, Q54, Q55, Q56, Q57, Q58, Q59, Q60, Q61, Q62]), "operationType" : NewBodyOperationType.REMOVE, "oppositeDirection" : true, "depth" : 0.5 * mm});
        }
        {
            var Q0;
            {var subQ0=sQuery(id+"F0.wireOp",EDGE,"E0");var subQ1=sQuery(id+"F2.wireOp",EDGE,"E3.7.1");var subQ2=sQuery(id+"F2.wireOp",EDGE,"E2.0.0");Q0=makeQuery(id+"F3.boolean.opBoolean","SPLIT",FACE,{"disambiguationData":[TD([makeQuery(id+"F3.opExtrude","SWEPT_FACE",FACE,{"disambiguationData":[OSD([subQ1]),TDD([makeQuery(id+"F2.imprint","IMPRINT",EDGE,{"disambiguationData":[TD([[makeQuery(id+"F2.imprint","INTERSECT",VERTEX,{"disambiguationData":[OD(0.0)],"derivedFrom":[subQ2,subQ1]}),-1.0]])],"derivedFrom":subQ1})])]})])],"derivedFrom":makeQuery(id+"F1.opExtrude","CAP_FACE",FACE,{"disambiguationData":[OSD([subQ0])],"isStart":false})});}
            var Q1;
            {var subQ0=sQuery(id+"F0.wireOp",EDGE,"E0");var subQ2=sQuery(id+"F2.wireOp",EDGE,"E2.0.0");var subQ3=sQuery(id+"F2.wireOp",EDGE,"E3.7.0");Q1=makeQuery(id+"F3.boolean.opBoolean","SPLIT",FACE,{"disambiguationData":[TD([makeQuery(id+"F3.opExtrude","SWEPT_FACE",FACE,{"disambiguationData":[OSD([subQ3]),TDD([makeQuery(id+"F2.imprint","IMPRINT",EDGE,{"disambiguationData":[TD([[makeQuery(id+"F2.imprint","INTERSECT",VERTEX,{"disambiguationData":[OD(0.0)],"derivedFrom":[subQ2,subQ3]}),-1.0]])],"derivedFrom":subQ3})])]})])],"derivedFrom":makeQuery(id+"F1.opExtrude","CAP_FACE",FACE,{"disambiguationData":[OSD([subQ0])],"isStart":false})});}
            var Q2;
            {var subQ0=sQuery(id+"F0.wireOp",EDGE,"E0");var subQ2=sQuery(id+"F2.wireOp",EDGE,"E2.0.0");var subQ3=sQuery(id+"F2.wireOp",EDGE,"E3.11.0");Q2=makeQuery(id+"F3.boolean.opBoolean","SPLIT",FACE,{"disambiguationData":[TD([makeQuery(id+"F3.opExtrude","SWEPT_FACE",FACE,{"disambiguationData":[OSD([subQ3]),TDD([makeQuery(id+"F2.imprint","IMPRINT",EDGE,{"disambiguationData":[TD([[makeQuery(id+"F2.imprint","INTERSECT",VERTEX,{"disambiguationData":[OD(1.0)],"derivedFrom":[subQ2,subQ3]}),1.0]])],"derivedFrom":subQ3})])]})])],"derivedFrom":makeQuery(id+"F1.opExtrude","CAP_FACE",FACE,{"disambiguationData":[OSD([subQ0])],"isStart":false})});}
            var Q3;
            {var subQ0=sQuery(id+"F0.wireOp",EDGE,"E0");var subQ1=sQuery(id+"F2.wireOp",EDGE,"E3.10.0");var subQ2=sQuery(id+"F2.wireOp",EDGE,"E2.0.0");Q3=makeQuery(id+"F3.boolean.opBoolean","SPLIT",FACE,{"disambiguationData":[TD([makeQuery(id+"F3.opExtrude","SWEPT_FACE",FACE,{"disambiguationData":[OSD([subQ1]),TDD([makeQuery(id+"F2.imprint","IMPRINT",EDGE,{"disambiguationData":[TD([[makeQuery(id+"F2.imprint","INTERSECT",VERTEX,{"disambiguationData":[OD(1.0)],"derivedFrom":[subQ2,subQ1]}),1.0]])],"derivedFrom":subQ1})])]})])],"derivedFrom":makeQuery(id+"F1.opExtrude","CAP_FACE",FACE,{"disambiguationData":[OSD([subQ0])],"isStart":false})});}
            var Q4;
            {var subQ0=sQuery(id+"F0.wireOp",EDGE,"E0");var subQ1=sQuery(id+"F2.wireOp",EDGE,"E3.9.0");var subQ2=sQuery(id+"F2.wireOp",EDGE,"E2.0.0");Q4=makeQuery(id+"F3.boolean.opBoolean","SPLIT",FACE,{"disambiguationData":[TD([makeQuery(id+"F3.opExtrude","SWEPT_FACE",FACE,{"disambiguationData":[OSD([subQ1]),TDD([makeQuery(id+"F2.imprint","IMPRINT",EDGE,{"disambiguationData":[TD([[makeQuery(id+"F2.imprint","INTERSECT",VERTEX,{"disambiguationData":[OD(1.0)],"derivedFrom":[subQ2,subQ1]}),1.0]])],"derivedFrom":subQ1})])]})])],"derivedFrom":makeQuery(id+"F1.opExtrude","CAP_FACE",FACE,{"disambiguationData":[OSD([subQ0])],"isStart":false})});}
            var Q5;
            {var subQ0=sQuery(id+"F0.wireOp",EDGE,"E0");var subQ1=sQuery(id+"F2.wireOp",EDGE,"E3.8.0");var subQ2=sQuery(id+"F2.wireOp",EDGE,"E2.0.0");Q5=makeQuery(id+"F3.boolean.opBoolean","SPLIT",FACE,{"disambiguationData":[TD([makeQuery(id+"F3.opExtrude","SWEPT_FACE",FACE,{"disambiguationData":[OSD([subQ1]),TDD([makeQuery(id+"F2.imprint","IMPRINT",EDGE,{"disambiguationData":[TD([[makeQuery(id+"F2.imprint","INTERSECT",VERTEX,{"disambiguationData":[OD(1.0)],"derivedFrom":[subQ2,subQ1]}),1.0]])],"derivedFrom":subQ1})])]})])],"derivedFrom":makeQuery(id+"F1.opExtrude","CAP_FACE",FACE,{"disambiguationData":[OSD([subQ0])],"isStart":false})});}
            var Q6;
            {var subQ0=sQuery(id+"F0.wireOp",EDGE,"E0");var subQ2=sQuery(id+"F2.wireOp",EDGE,"E2.0.0");var subQ3=sQuery(id+"F2.wireOp",EDGE,"E3.7.0");Q6=makeQuery(id+"F3.boolean.opBoolean","SPLIT",FACE,{"disambiguationData":[TD([makeQuery(id+"F3.opExtrude","SWEPT_FACE",FACE,{"disambiguationData":[OSD([subQ3]),TDD([makeQuery(id+"F2.imprint","IMPRINT",EDGE,{"disambiguationData":[TD([[makeQuery(id+"F2.imprint","INTERSECT",VERTEX,{"disambiguationData":[OD(1.0)],"derivedFrom":[subQ2,subQ3]}),1.0]])],"derivedFrom":subQ3})])]})])],"derivedFrom":makeQuery(id+"F1.opExtrude","CAP_FACE",FACE,{"disambiguationData":[OSD([subQ0])],"isStart":false})});}
            var Q7;
            {var subQ0=sQuery(id+"F0.wireOp",EDGE,"E0");var subQ2=sQuery(id+"F2.wireOp",EDGE,"E2.0.0");var subQ3=sQuery(id+"F2.wireOp",EDGE,"E3.7.1");Q7=makeQuery(id+"F3.boolean.opBoolean","SPLIT",FACE,{"disambiguationData":[TD([makeQuery(id+"F3.opExtrude","SWEPT_FACE",FACE,{"disambiguationData":[OSD([subQ3]),TDD([makeQuery(id+"F2.imprint","IMPRINT",EDGE,{"disambiguationData":[TD([[makeQuery(id+"F2.imprint","INTERSECT",VERTEX,{"disambiguationData":[OD(1.0)],"derivedFrom":[subQ2,subQ3]}),1.0]])],"derivedFrom":subQ3})])]})])],"derivedFrom":makeQuery(id+"F1.opExtrude","CAP_FACE",FACE,{"disambiguationData":[OSD([subQ0])],"isStart":false})});}
            var Q8;
            {var subQ0=sQuery(id+"F0.wireOp",EDGE,"E0");var subQ2=sQuery(id+"F2.wireOp",EDGE,"E2.0.0");var subQ3=sQuery(id+"F2.wireOp",EDGE,"E3.11.1");Q8=makeQuery(id+"F3.boolean.opBoolean","SPLIT",FACE,{"disambiguationData":[TD([makeQuery(id+"F3.opExtrude","SWEPT_FACE",FACE,{"disambiguationData":[OSD([subQ3]),TDD([makeQuery(id+"F2.imprint","IMPRINT",EDGE,{"disambiguationData":[TD([[makeQuery(id+"F2.imprint","INTERSECT",VERTEX,{"disambiguationData":[OD(0.0)],"derivedFrom":[subQ2,subQ3]}),-1.0]])],"derivedFrom":subQ3})])]})])],"derivedFrom":makeQuery(id+"F1.opExtrude","CAP_FACE",FACE,{"disambiguationData":[OSD([subQ0])],"isStart":false})});}
            var Q9;
            {var subQ0=sQuery(id+"F0.wireOp",EDGE,"E0");var subQ1=sQuery(id+"F2.wireOp",EDGE,"E3.10.1");var subQ2=sQuery(id+"F2.wireOp",EDGE,"E2.0.0");Q9=makeQuery(id+"F3.boolean.opBoolean","SPLIT",FACE,{"disambiguationData":[TD([makeQuery(id+"F3.opExtrude","SWEPT_FACE",FACE,{"disambiguationData":[OSD([subQ1]),TDD([makeQuery(id+"F2.imprint","IMPRINT",EDGE,{"disambiguationData":[TD([[makeQuery(id+"F2.imprint","INTERSECT",VERTEX,{"disambiguationData":[OD(0.0)],"derivedFrom":[subQ2,subQ1]}),-1.0]])],"derivedFrom":subQ1})])]})])],"derivedFrom":makeQuery(id+"F1.opExtrude","CAP_FACE",FACE,{"disambiguationData":[OSD([subQ0])],"isStart":false})});}
            var Q10;
            {var subQ0=sQuery(id+"F0.wireOp",EDGE,"E0");var subQ1=sQuery(id+"F2.wireOp",EDGE,"E3.9.1");var subQ2=sQuery(id+"F2.wireOp",EDGE,"E2.0.0");Q10=makeQuery(id+"F3.boolean.opBoolean","SPLIT",FACE,{"disambiguationData":[TD([makeQuery(id+"F3.opExtrude","SWEPT_FACE",FACE,{"disambiguationData":[OSD([subQ1]),TDD([makeQuery(id+"F2.imprint","IMPRINT",EDGE,{"disambiguationData":[TD([[makeQuery(id+"F2.imprint","INTERSECT",VERTEX,{"disambiguationData":[OD(0.0)],"derivedFrom":[subQ2,subQ1]}),-1.0]])],"derivedFrom":subQ1})])]})])],"derivedFrom":makeQuery(id+"F1.opExtrude","CAP_FACE",FACE,{"disambiguationData":[OSD([subQ0])],"isStart":false})});}
            var Q11;
            {var subQ0=sQuery(id+"F0.wireOp",EDGE,"E0");var subQ1=sQuery(id+"F2.wireOp",EDGE,"E3.8.1");var subQ2=sQuery(id+"F2.wireOp",EDGE,"E2.0.0");Q11=makeQuery(id+"F3.boolean.opBoolean","SPLIT",FACE,{"disambiguationData":[TD([makeQuery(id+"F3.opExtrude","SWEPT_FACE",FACE,{"disambiguationData":[OSD([subQ1]),TDD([makeQuery(id+"F2.imprint","IMPRINT",EDGE,{"disambiguationData":[TD([[makeQuery(id+"F2.imprint","INTERSECT",VERTEX,{"disambiguationData":[OD(0.0)],"derivedFrom":[subQ2,subQ1]}),-1.0]])],"derivedFrom":subQ1})])]})])],"derivedFrom":makeQuery(id+"F1.opExtrude","CAP_FACE",FACE,{"disambiguationData":[OSD([subQ0])],"isStart":false})});}
            chamfer(context, id + "F4", {"entities" : qUnion([Q0, Q1, Q2, Q3, Q4, Q5, Q6, Q7, Q8, Q9, Q10, Q11]), "width" : 0.5 * mm, "tangentPropagation" : true});
        }
    });
